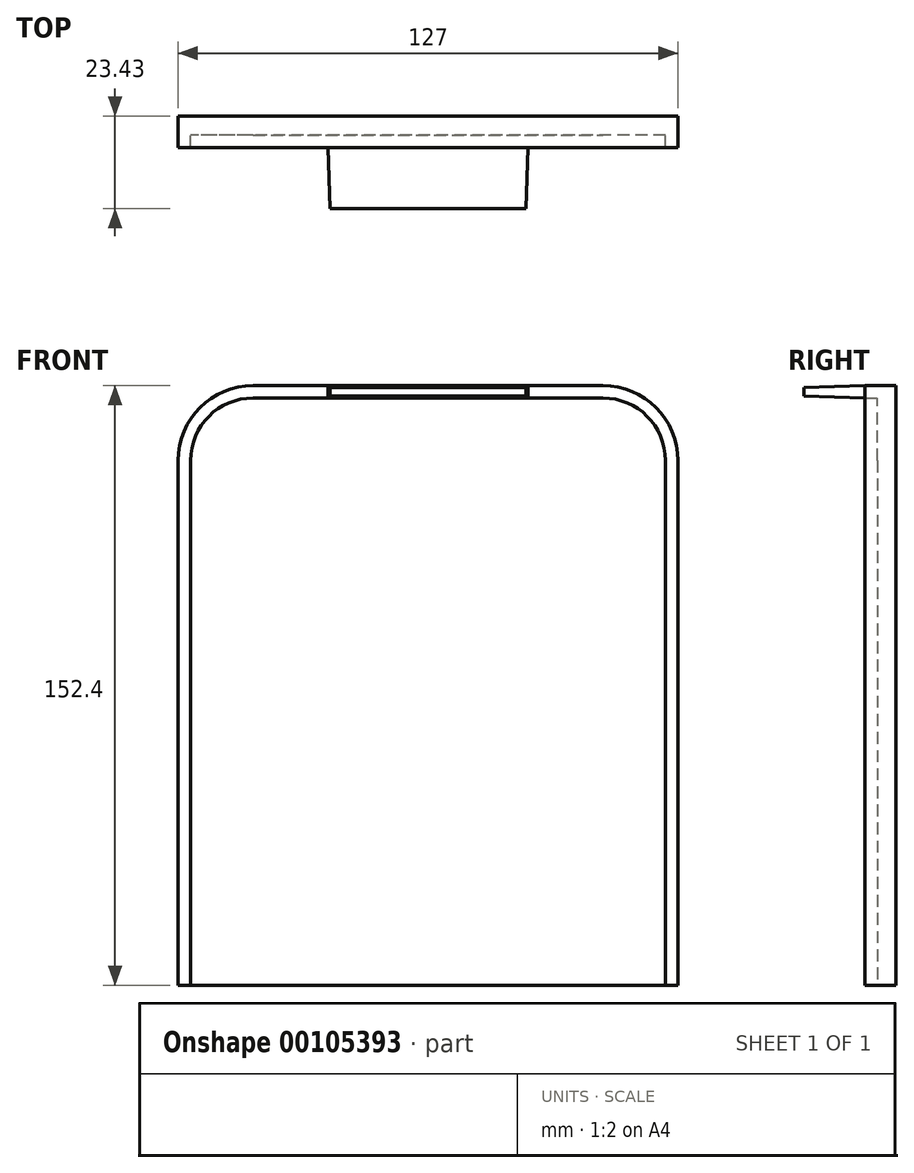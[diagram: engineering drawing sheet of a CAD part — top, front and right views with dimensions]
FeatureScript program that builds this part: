
annotation { "Feature Type Name" : "Feature", "Feature Type Description" : "" }
export const myFeature = defineFeature(function(context is Context, id is Id, definition is map)
    precondition{}
    {
        {
            var Q0;
            Q0=qCreatedBy(makeId("Front.planeOp"),FACE);
            var sketch = newSketch(context, id + "F0", { "sketchPlane" : qUnion([Q0])});
            skLineSegment(sketch, "E0.bottom", {"start": v(63.5, -76.2) * mm, "end": v(-63.5, -76.2) * mm});
            skLineSegment(sketch, "E0.top", {"start": v(44.45, 76.2) * mm, "end": v(-44.45, 76.2) * mm});
            skLineSegment(sketch, "E0.left", {"start": v(63.5, -76.2) * mm, "end": v(63.5, 57.15) * mm});
            skLineSegment(sketch, "E0.right", {"start": v(-63.5, -76.2) * mm, "end": v(-63.5, 57.15) * mm});
            skPoint(sketch, "E0.middle", {"position": v(0, 0) * mm});
            skPoint(sketch, "E1.visualSharp", {"position": v(-63.5, 76.2) * mm});
            skArc(sketch, "E1.filletArc", {"start": v(-44.45, 76.2) * mm, "mid": v(-57.92, 70.62) * mm, "end": v(-63.5, 57.15) * mm});
            skPoint(sketch, "E2.visualSharp", {"position": v(63.5, 76.2) * mm});
            skArc(sketch, "E2.filletArc", {"start": v(63.5, 57.15) * mm, "mid": v(57.92, 70.62) * mm, "end": v(44.45, 76.2) * mm});
            skSolve(sketch);
        }
        {
            var Q0;
            Q0 = qSketchRegion(id + "F0", true);
            extrude(context, id + "F1", {"entities" : qUnion([Q0]), "depth" : 4.76 * mm, "hasDraft" : true, "draftAngle" : 0 * degree});
        }
        {
            var Q0;
            Q0=makeQuery(id+"F1.opExtrude","CAP_FACE",FACE,{"disambiguationData":[OSD([sQuery(id+"F0.wireOp",EDGE,"E0.bottom"),sQuery(id+"F0.wireOp",EDGE,"E0.top"),sQuery(id+"F0.wireOp",EDGE,"E0.left"),sQuery(id+"F0.wireOp",EDGE,"E0.right"),sQuery(id+"F0.wireOp",EDGE,"E1.filletArc"),sQuery(id+"F0.wireOp",EDGE,"E2.filletArc")])],"isStart":true});
            var sketch = newSketch(context, id + "F2", { "sketchPlane" : qUnion([Q0])});
            skArc(sketch, "E3.0.0", {"start": v(-63.5, 57.15) * mm, "mid": v(-57.92, 70.62) * mm, "end": v(-44.45, 76.2) * mm});
            skLineSegment(sketch, "E3.0.1", {"start": v(-44.45, 76.2) * mm, "end": v(44.45, 76.2) * mm});
            skArc(sketch, "E3.0.2", {"start": v(44.45, 76.2) * mm, "mid": v(57.92, 70.62) * mm, "end": v(63.5, 57.15) * mm});
            skLineSegment(sketch, "E3.0.3", {"start": v(63.5, 57.15) * mm, "end": v(63.5, -76.2) * mm});
            skLineSegment(sketch, "E3.0.5", {"start": v(-63.5, -76.2) * mm, "end": v(-63.5, 57.15) * mm});
            skLineSegment(sketch, "E4.0", {"start": v(-44.45, 73.03) * mm, "end": v(44.45, 73.03) * mm});
            skLineSegment(sketch, "E4.1", {"start": v(-60.33, -76.2) * mm, "end": v(-60.33, 57.15) * mm});
            skArc(sketch, "E4.3", {"start": v(-44.45, 73.03) * mm, "mid": v(-55.68, 68.38) * mm, "end": v(-60.33, 57.15) * mm});
            skLineSegment(sketch, "E4.4", {"start": v(60.32, -76.2) * mm, "end": v(60.32, 57.15) * mm});
            skArc(sketch, "E4.5", {"start": v(60.32, 57.15) * mm, "mid": v(55.68, 68.38) * mm, "end": v(44.45, 73.03) * mm});
            skLineSegment(sketch, "E5", {"start": v(63.5, -76.2) * mm, "end": v(60.32, -76.2) * mm});
            skLineSegment(sketch, "E6", {"start": v(-60.33, -76.2) * mm, "end": v(-63.5, -76.2) * mm});
            skSolve(sketch);
        }
        {
            var Q0;
            Q0 = qSketchRegion(id + "F2", true);
            extrude(context, id + "F3", {"entities" : qUnion([Q0]), "operationType" : NewBodyOperationType.ADD, "oppositeDirection" : true, "depth" : 7.94 * mm});
        }
        {
            var Q0;
            Q0=makeQuery(id+"F3.opExtrude","CAP_FACE",FACE,{"disambiguationData":[OSD([sQuery(id+"F2.wireOp",EDGE,"E3.0.0"),sQuery(id+"F2.wireOp",EDGE,"E3.0.1"),sQuery(id+"F2.wireOp",EDGE,"E3.0.2"),sQuery(id+"F2.wireOp",EDGE,"E3.0.3"),sQuery(id+"F2.wireOp",EDGE,"E3.0.5"),sQuery(id+"F2.wireOp",EDGE,"E4.0"),sQuery(id+"F2.wireOp",EDGE,"E4.1"),sQuery(id+"F2.wireOp",EDGE,"E4.3"),sQuery(id+"F2.wireOp",EDGE,"E4.4"),sQuery(id+"F2.wireOp",EDGE,"E4.5"),sQuery(id+"F2.wireOp",EDGE,"E5"),sQuery(id+"F2.wireOp",EDGE,"E6")])],"isStart":false});
            var sketch = newSketch(context, id + "F4", { "sketchPlane" : qUnion([Q0])});
            skLineSegment(sketch, "E7.bottom", {"start": v(-25.4, 76.2) * mm, "end": v(25.4, 76.2) * mm});
            skLineSegment(sketch, "E7.top", {"start": v(-25.4, 73.03) * mm, "end": v(25.4, 73.03) * mm});
            skLineSegment(sketch, "E7.left", {"start": v(-25.4, 76.2) * mm, "end": v(-25.4, 73.03) * mm});
            skLineSegment(sketch, "E7.right", {"start": v(25.4, 76.2) * mm, "end": v(25.4, 73.03) * mm});
            skLineSegment(sketch, "E8", {"start": v(0, 73.03) * mm, "end": v(0, 76.2) * mm, "construction": true});
            skSolve(sketch);
        }
        {
            var Q0;
            Q0 = qSketchRegion(id + "F4", true);
            extrude(context, id + "F5", {"entities" : qUnion([Q0]), "operationType" : NewBodyOperationType.ADD, "depth" : 15.5 * mm, "hasDraft" : true, "draftAngle" : 2 * degree, "draftPullDirection" : true});
        }
    });
